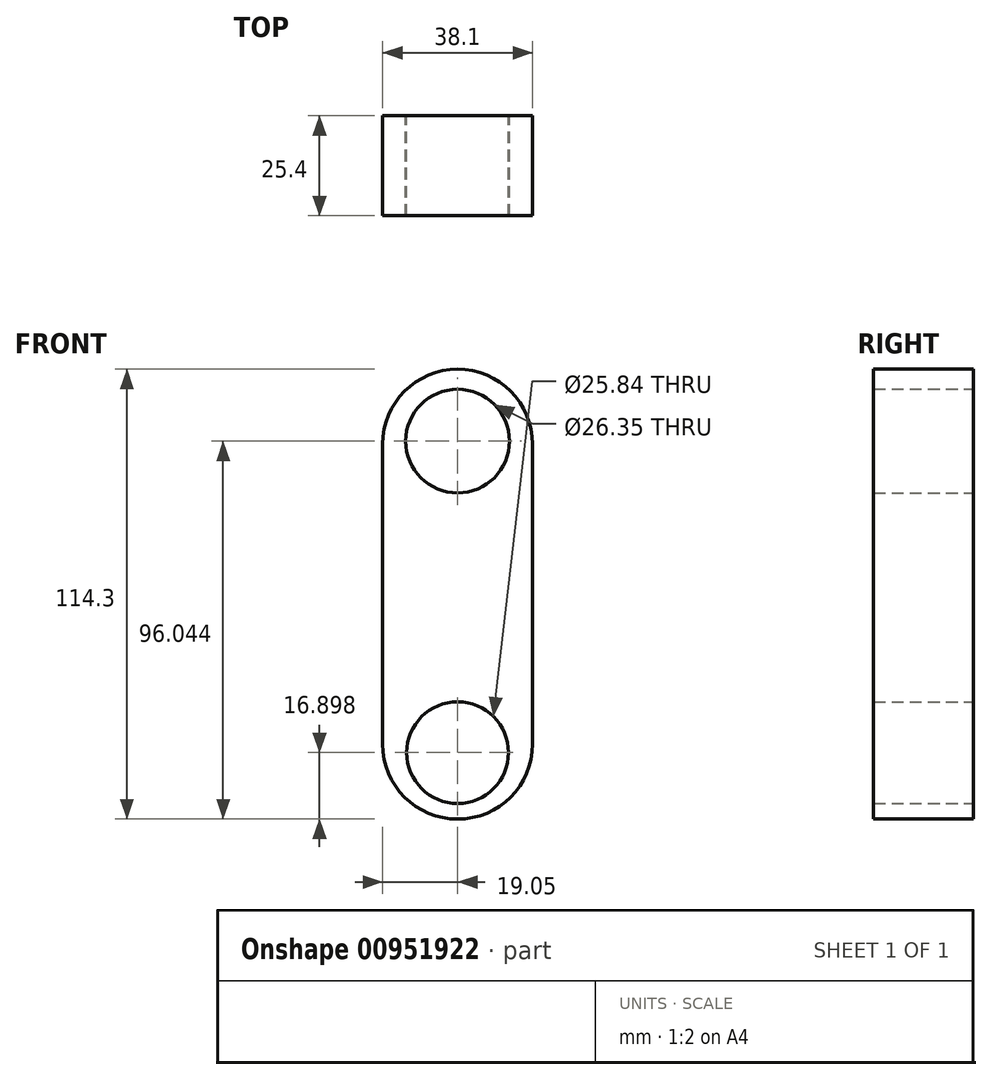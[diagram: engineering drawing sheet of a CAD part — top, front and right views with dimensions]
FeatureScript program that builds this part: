
annotation { "Feature Type Name" : "Feature", "Feature Type Description" : "" }
export const myFeature = defineFeature(function(context is Context, id is Id, definition is map)
    precondition{}
    {
        {
            var Q0;
            Q0=qCreatedBy(makeId("Front.planeOp"),FACE);
            var sketch = newSketch(context, id + "F0", { "sketchPlane" : qUnion([Q0])});
            skLineSegment(sketch, "E0.bottom", {"start": v(-19.05, 38.1) * mm, "end": v(19.05, 38.1) * mm});
            skLineSegment(sketch, "E0.top", {"start": v(-19.05, -38.1) * mm, "end": v(19.05, -38.1) * mm});
            skLineSegment(sketch, "E0.left", {"start": v(-19.05, 38.1) * mm, "end": v(-19.05, -38.1) * mm});
            skLineSegment(sketch, "E0.right", {"start": v(19.05, 38.1) * mm, "end": v(19.05, -38.1) * mm});
            skCircle(sketch, "E1", {"center": v(0, 38.1) * mm, "radius": 19.05 * mm});
            skCircle(sketch, "E2", {"center": v(0, -38.1) * mm, "radius": 19.05 * mm});
            skSolve(sketch);
        }
        {
            var Q0;
            Q0 = qSketchRegion(id + "F0", true);
            extrude(context, id + "F1", {"entities" : qUnion([Q0]), "depth" : 25.4 * mm, "offsetDistance" : 25.4 * mm});
        }
        {
            var Q0;
            Q0=qCreatedBy(makeId("Front.planeOp"),FACE);
            var sketch = newSketch(context, id + "F2", { "sketchPlane" : qUnion([Q0])});
            skCircle(sketch, "E3", {"center": v(0, 38.9) * mm, "radius": 13.17 * mm});
            skCircle(sketch, "E4", {"center": v(0, -40.25) * mm, "radius": 12.92 * mm});
            skSolve(sketch);
        }
        {
            var Q0;
            Q0 = qSketchRegion(id + "F2", true);
            extrude(context, id + "F3", {"entities" : qUnion([Q0]), "operationType" : NewBodyOperationType.REMOVE, "depth" : 100.58 * mm, "offsetDistance" : 25.4 * mm});
        }
    });
